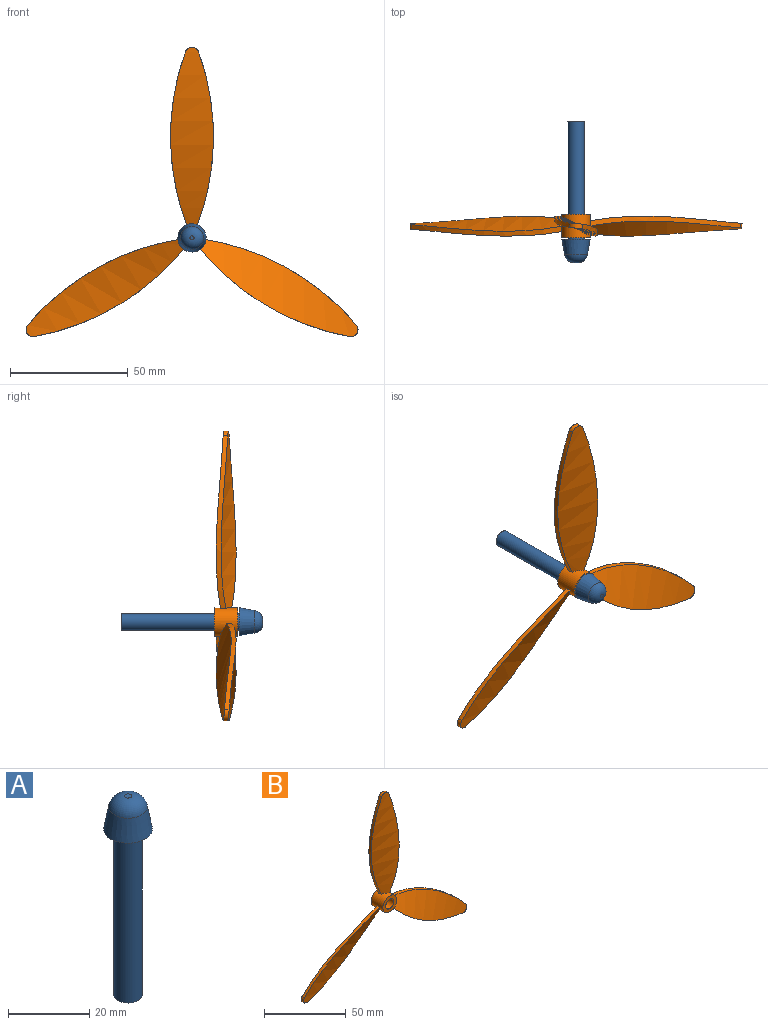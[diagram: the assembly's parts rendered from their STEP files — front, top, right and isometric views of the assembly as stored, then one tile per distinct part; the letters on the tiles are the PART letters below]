
ASSEMBLY  parts=2 mates=1
PART A: 6 faces, bbox 12x12x60 mm
  f0: cylinder r=3.5mm len=50mm, axis (0,0,-1), area 1099.6mm2, adj f1,f4
  f1: plane 7x7mm, normal (0,0,-1), area 38.5mm2, adj f0
  f2: cone r=6mm half-angle=10deg, axis (0,0,-1), area 231.1mm2, adj f4,f5
  f3: plane 1.76x1.76mm, normal (0,0,1), area 2.4mm2, adj f5
  f4: plane 12x12mm, normal (0,0,-1), area 74.6mm2, adj f0,f2
  f5: torus R=0.88mm, axis (0,0,1), area 114mm2, adj f2,f3
PART B: 19 faces, bbox 188.2x16.7x163 mm
  f0: cylinder r=106mm len=73.47mm, axis (0,-1,0), area 154.2mm2, adj f2,f3,f4,f5
  f1: cylinder r=106mm len=73.47mm, axis (0,-1,0), area 154.2mm2, adj f2,f3,f4,f5
  f2: bspline ~100x30mm, area 1083.3mm2, adj f0,f1,f4,f5
  f3: bspline ~100x30mm, area 1083.3mm2, adj f0,f1,f4,f5
  f4: cylinder r=3mm len=5.64mm, axis (0,-1,0), area 14.4mm2, adj f0,f1,f2,f3
  f5: cylinder r=6mm len=12mm, axis (0,1,0), area 345.3mm2, adj f0,f1,f2,f3,f6,f7,f8,f9
  f6: plane 12x12mm, normal (0,-1,0), area 74.6mm2, adj f5,f18
  f7: plane 12x12mm, normal (0,1,0), area 74.6mm2, adj f5,f18
  f8: cylinder r=106mm len=63.35mm, axis (0,-1,0), area 154.2mm2, adj f5,f10,f11,f12
  f9: cylinder r=106mm len=63.9mm, axis (0,-1,0), area 154.2mm2, adj f5,f10,f11,f12
  f10: bspline ~100.35x74.67mm, area 1083.3mm2, adj f5,f8,f9,f12
  f11: bspline ~100.85x73.81mm, area 1083.3mm2, adj f5,f8,f9,f12
  f12: cylinder r=3mm len=4.93mm, axis (0,-1,0), area 14.4mm2, adj f8,f9,f10,f11
  f13: cylinder r=106mm len=63.9mm, axis (0,-1,0), area 154.2mm2, adj f5,f15,f16,f17
  f14: cylinder r=106mm len=63.35mm, axis (0,-1,0), area 154.2mm2, adj f5,f15,f16,f17
  f15: bspline ~100.85x73.81mm, area 1083.3mm2, adj f5,f13,f14,f17
  f16: bspline ~100.35x74.67mm, area 1083.3mm2, adj f5,f13,f14,f17
  f17: cylinder r=3mm len=4.93mm, axis (0,-1,0), area 14.4mm2, adj f13,f14,f15,f16
  f18: cylinder r=3.5mm len=10mm, axis (0,-1,0), area 219.9mm2, adj f6,f7
PLACE A rot(axis=(1,0,0),90deg) t=(-11.88,14.07,-25.5)mm
PLACE B t=(-11.88,-30.43,-25.5)mm
MATE revolute B.f18 <-> A.f0  axis (0,-1,0) through (-11.88,-35.43,-25.5)mm
